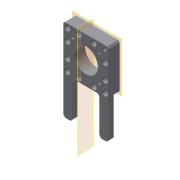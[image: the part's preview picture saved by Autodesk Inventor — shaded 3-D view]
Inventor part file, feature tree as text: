
AUTODESK INVENTOR PART (.ipt)
format: ipt  version: 2019.4 (Build 234330000, 330)  size: 276,480 bytes
history: native  units: mm
features: other x6, extrude x5, sketch x5, reference x4, projected_geometry x4, plane x2, fillet x1, hole x1, chamfer x1
ambient origin geometry x8: Origin, YZ Plane, XZ Plane, XY Plane, X Axis, Y Axis, Z Axis, Center Point
bodies: Solid1 (feature_tree)
feature tree (29):
  plane  "Work Plane1"
  extrude  "Extrusion1"  Depth=7.0mm TaperAngle=0.0deg
  extrude  "Extrusion2"  Depth=4.0mm
  fillet  "Fillet1"  Radius=4.0mm
  extrude  "Extrusion6"  Depth=8.0mm
  plane  "Work Plane2"
  hole  "Hole1"  [1 undecoded]
  extrude  "Extrusion7"  Depth=12.0mm
  chamfer  "Chamfer3"  Distance=5.0mm Angle=45.0deg
  extrude  "Extrusion9"  Depth=6.0mm
  sketch  "Sketch1"  dims[d1=8.0mm d2=0.0mm d6=7.0mm d7=0.0mm]
  reference  "Reference1"
  reference  "Reference2"
  projected_geometry  "Projected Loop1"
  sketch  "Sketch6"  dims[d12=4.0mm d27=4.9mm d28=4.0mm d29=0.0mm]
  projected_geometry  "Projected Loop5"
  reference  "Reference4"
  sketch  "Sketch7"  dims[d31=3.2mm d32=6.0mm d33=8.0mm d34=10.0mm d35=90.0deg d36=8.0mm d37=20.594885mm d41=32.0mm]
  reference  "Reference5"
  sketch  "Sketch8"  dims[d42=4.0mm d43=0.0mm d57=12.0mm]
  sketch  "Sketch10"  dims[d58=50.0mm d59=12.0mm d60=5.0mm d61=2.0mm d62=45.0deg d63=4.9mm d64=4.9mm d65=4.9mm d66=4.9mm d67=4.9mm d68=4.9mm d69=10.0mm d70=12.0mm d71=12.0mm d72=10.0mm d73=12.0mm d74=12.0mm d75=6.0mm d76=0.0mm]
  projected_geometry  "Projected Loop7"
  projected_geometry  "Projected Loop8"
  other  "Application_Fluorescence_Microscope_Infinity_cellstorm_v3.iam"
  other  "00_XY_stage-CHUO_SEIKI_LD-647-R1:1"
  other  "00_XY_stage-CHUO_SEIKI_LD-647-R1-Top:1"
  other  "00_Microscope_Objective:1"
  other  "cellSTORM_UC2_Sample.iam"
  other  "cellSTORM_inverted_chiptray_v0:1"
note: 1 required parameter value undecoded (feature->parameter linkage not recoverable at this tier; creation-order binding heuristic only, values carry confidence <= 0.55)
